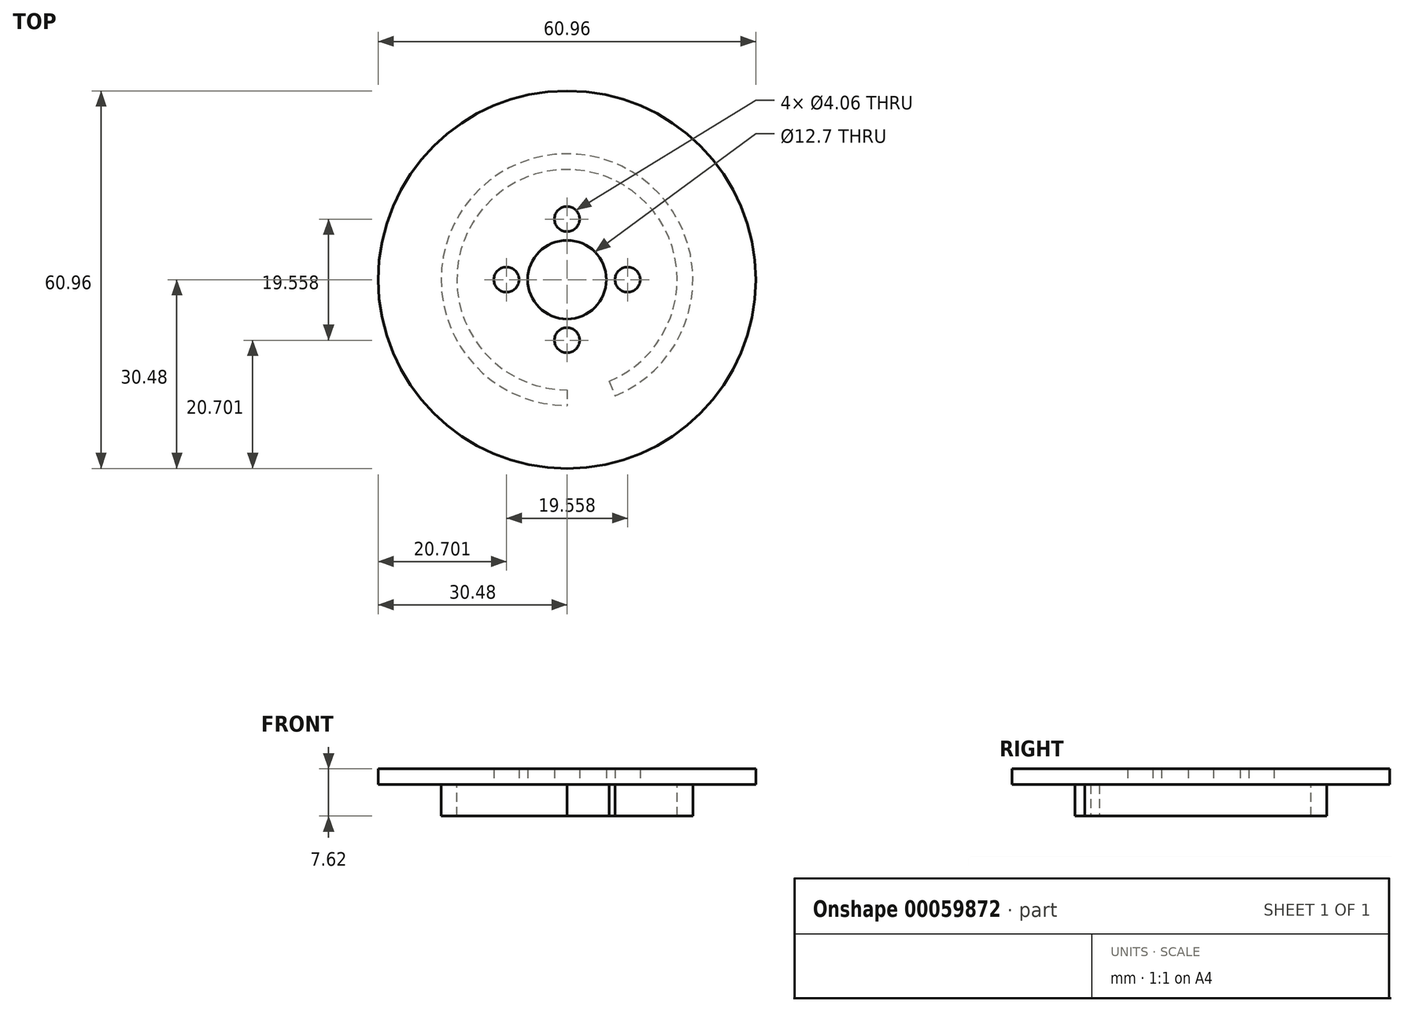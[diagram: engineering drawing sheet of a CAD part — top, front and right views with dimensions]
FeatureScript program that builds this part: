
annotation { "Feature Type Name" : "Feature", "Feature Type Description" : "" }
export const myFeature = defineFeature(function(context is Context, id is Id, definition is map)
    precondition{}
    {
        {
            var Q0;
            Q0=qCreatedBy(makeId("Top.planeOp"),FACE);
            var sketch = newSketch(context, id + "F0", { "sketchPlane" : qUnion([Q0])});
            skCircle(sketch, "E0", {"center": v(0, 0) * mm, "radius": 6.35 * mm});
            skCircle(sketch, "E1", {"center": v(0, 0) * mm, "radius": 30.48 * mm});
            skLineSegment(sketch, "E2", {"start": v(0, 0) * mm, "end": v(0, 9.78) * mm});
            skLineSegment(sketch, "E3", {"start": v(0, 0) * mm, "end": v(9.78, 0) * mm});
            skLineSegment(sketch, "E4", {"start": v(0, 0) * mm, "end": v(0, -9.78) * mm});
            skLineSegment(sketch, "E5", {"start": v(0, 0) * mm, "end": v(-9.78, 0) * mm});
            skCircle(sketch, "E6", {"center": v(-9.78, 0) * mm, "radius": 2.03 * mm});
            skCircle(sketch, "E7", {"center": v(0, 9.78) * mm, "radius": 2.03 * mm});
            skCircle(sketch, "E8", {"center": v(9.78, 0) * mm, "radius": 2.03 * mm});
            skCircle(sketch, "E9", {"center": v(0, -9.78) * mm, "radius": 2.03 * mm});
            skCircle(sketch, "E10", {"center": v(0, 9.78) * mm, "radius": 2.92 * mm});
            skCircle(sketch, "E11", {"center": v(9.78, 0) * mm, "radius": 2.92 * mm});
            skCircle(sketch, "E12", {"center": v(-9.78, 0) * mm, "radius": 2.92 * mm});
            skCircle(sketch, "E13", {"center": v(0, -9.78) * mm, "radius": 2.92 * mm});
            skSolve(sketch);
        }
        {
            var Q0;
            Q0 = qSketchRegion(id + "F0", true);
            var Q1;
            Q1=makeQuery(id+"F0.imprint","IMPRINT",FACE,{"disambiguationData":[TD([[makeQuery(id+"F0.imprint","IMPRINT",EDGE,{"derivedFrom":sQuery(id+"F0.wireOp",EDGE,"E7")}),-1.0]])]});
            var Q2;
            Q2=makeQuery(id+"F0.imprint","IMPRINT",FACE,{"disambiguationData":[TD([[makeQuery(id+"F0.imprint","IMPRINT",EDGE,{"derivedFrom":sQuery(id+"F0.wireOp",EDGE,"E6")}),-1.0]])]});
            var Q3;
            Q3=makeQuery(id+"F0.imprint","IMPRINT",FACE,{"disambiguationData":[TD([[makeQuery(id+"F0.imprint","IMPRINT",EDGE,{"derivedFrom":sQuery(id+"F0.wireOp",EDGE,"E9")}),-1.0]])]});
            var Q4;
            Q4=makeQuery(id+"F0.imprint","IMPRINT",FACE,{"disambiguationData":[TD([[makeQuery(id+"F0.imprint","IMPRINT",EDGE,{"derivedFrom":sQuery(id+"F0.wireOp",EDGE,"E8")}),-1.0]])]});
            extrude(context, id + "F1", {"entities" : qUnion([Q0, Q1, Q2, Q3, Q4]), "depth" : 2.54 * mm});
        }
        {
            var Q0;
            Q0=makeQuery(id+"F1.opExtrude","CAP_FACE",FACE,{"disambiguationData":[OSD([sQuery(id+"F0.wireOp",EDGE,"E0"),sQuery(id+"F0.wireOp",EDGE,"E1"),sQuery(id+"F0.wireOp",EDGE,"E6"),sQuery(id+"F0.wireOp",EDGE,"E7"),sQuery(id+"F0.wireOp",EDGE,"E8"),sQuery(id+"F0.wireOp",EDGE,"E9")])],"isStart":true});
            var sketch = newSketch(context, id + "F2", { "sketchPlane" : qUnion([Q0])});
            skCircle(sketch, "E14", {"center": v(0, 0) * mm, "radius": 20.32 * mm});
            skCircle(sketch, "E15", {"center": v(0, 0) * mm, "radius": 17.78 * mm});
            skSolve(sketch);
        }
        {
            var Q0;
            Q0=makeQuery(id+"F2.imprint","IMPRINT",FACE,{"disambiguationData":[TD([[makeQuery(id+"F2.imprint","IMPRINT",EDGE,{"derivedFrom":sQuery(id+"F2.wireOp",EDGE,"E14")}),1.0]])]});
            extrude(context, id + "F3", {"entities" : qUnion([Q0]), "operationType" : NewBodyOperationType.ADD, "depth" : 5.08 * mm});
        }
        {
            var Q0;
            Q0=makeQuery(id+"F3.opExtrude","CAP_FACE",FACE,{"disambiguationData":[OSD([sQuery(id+"F2.wireOp",EDGE,"E14"),sQuery(id+"F2.wireOp",EDGE,"E15")])],"isStart":false});
            var sketch = newSketch(context, id + "F4", { "sketchPlane" : qUnion([Q0])});
            skCircle(sketch, "E16", {"center": v(0, 0) * mm, "radius": 20.32 * mm});
            skCircle(sketch, "E17", {"center": v(0, 0) * mm, "radius": 17.78 * mm});
            skLineSegment(sketch, "E18", {"start": v(0, 0) * mm, "end": v(0, 20.32) * mm});
            skLineSegment(sketch, "E19", {"start": v(0, 0) * mm, "end": v(7.78, 18.77) * mm});
            skSolve(sketch);
        }
        {
            var Q0;
            {var subQ0=sQuery(id+"F4.wireOp",EDGE,"E18");var subQ1=sQuery(id+"F4.wireOp",EDGE,"E16");var subQ2=makeQuery(id+"F4.imprint","INTERSECT",VERTEX,{"derivedFrom":[subQ1,subQ0]});Q0=makeQuery(id+"F4.imprint","IMPRINT",FACE,{"disambiguationData":[TD([[makeQuery(id+"F4.imprint","IMPRINT",EDGE,{"disambiguationData":[TD([[subQ2,1.0]])],"derivedFrom":subQ1}),1.0]])]});}
            extrude(context, id + "F5", {"entities" : qUnion([Q0]), "operationType" : NewBodyOperationType.REMOVE, "oppositeDirection" : true, "depth" : 5.08 * mm});
        }
    });
